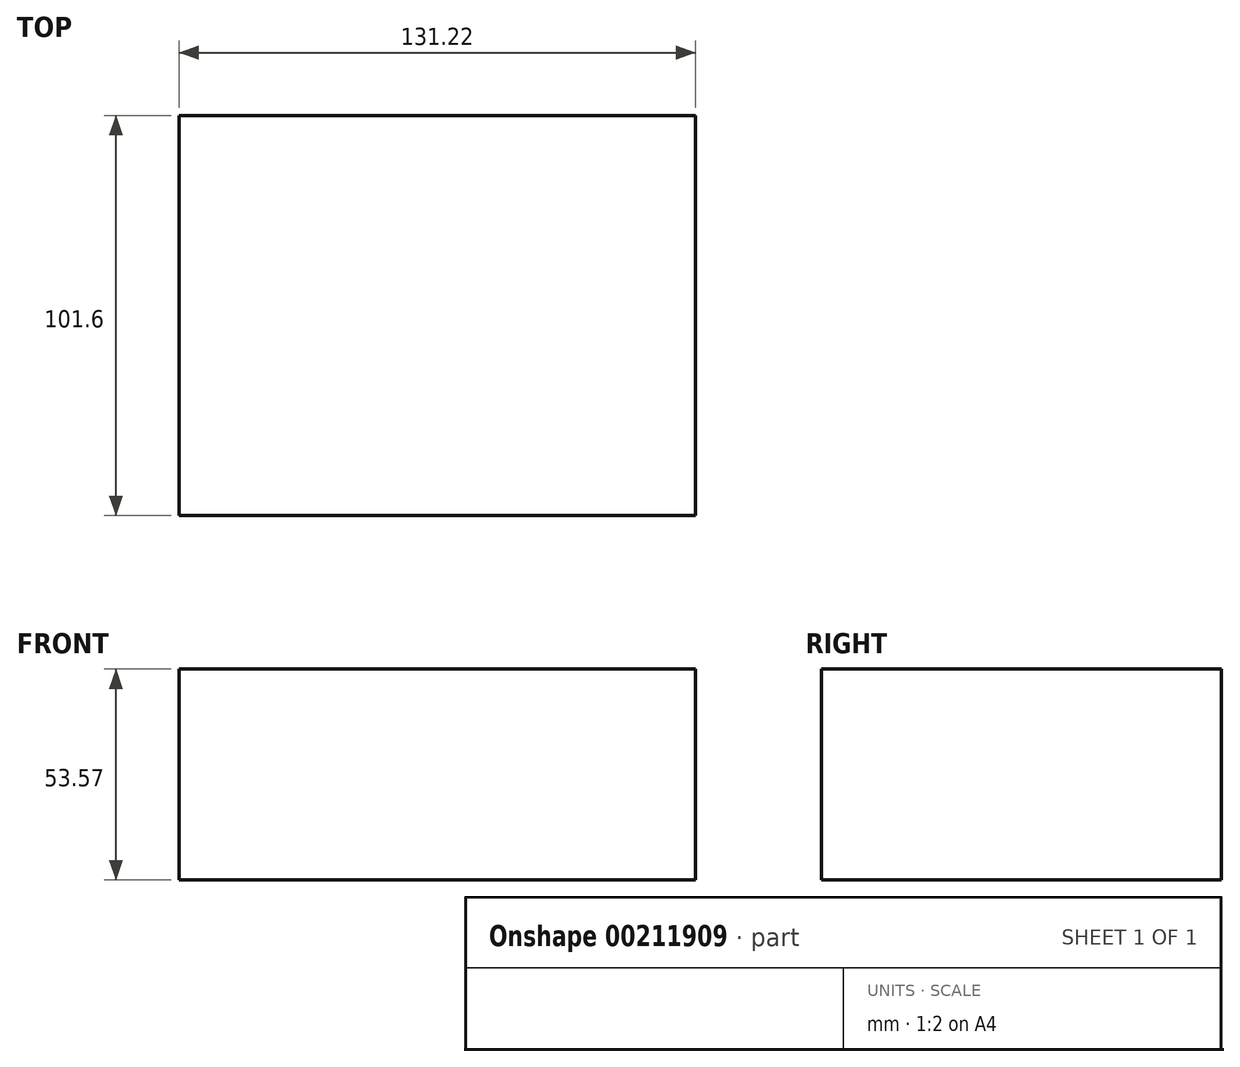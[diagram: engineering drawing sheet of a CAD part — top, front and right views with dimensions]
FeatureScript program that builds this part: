
annotation { "Feature Type Name" : "Feature", "Feature Type Description" : "" }
export const myFeature = defineFeature(function(context is Context, id is Id, definition is map)
    precondition{}
    {
        {
            var Q0;
            Q0=qCreatedBy(makeId("Front.planeOp"),FACE);
            var sketch = newSketch(context, id + "F0", { "sketchPlane" : qUnion([Q0])});
            skLineSegment(sketch, "E0.bottom", {"start": v(-67.5, 16.42) * mm, "end": v(63.72, 16.42) * mm});
            skLineSegment(sketch, "E0.top", {"start": v(-67.5, -37.15) * mm, "end": v(63.72, -37.15) * mm});
            skLineSegment(sketch, "E0.left", {"start": v(-67.5, 16.42) * mm, "end": v(-67.5, -37.15) * mm});
            skLineSegment(sketch, "E0.right", {"start": v(63.72, 16.42) * mm, "end": v(63.72, -37.15) * mm});
            skSolve(sketch);
        }
        {
            var Q0;
            Q0 = qSketchRegion(id + "F0", true);
            extrude(context, id + "F1", {"entities" : qUnion([Q0]), "depth" : 101.6 * mm});
        }
    });
